# Revit family: Nursing Bench 3000 height adjustable_v_1.0
name_source: partatom
category: Specialty Equipment
revit_build: Autodesk Revit Architecture 2012 (Build: 20110309_2315(x64)
units: mm (PartAtom-declared; Revit-internal decimal feet)

## types (4) — shared parameters
Adjustment Interval (Height) = 300 mm - 1000 mm above floor
Assembly Code = C1030200
Assembly Description = Bath & Toilet Accessories
Couch Elevation = 865 mm  [stored 2.83793 ft]
File Version = V 1.0
Manufacturer = Pressalit Care
OmniClass Number = 23.40.20.21
OmniClass Title = Toilet and Bath Specialties
URL = www.pressalitcare.com

## per-type parameters (varying)
| type | Bed Pattern 1300 | Bed Pattern 1800 | Description | Length | Model | Rail | With Safety Rail |
| Height adjustable nursing bench with safety rail, 1800 mm. Electric. | No | Yes | Nursing bench with safety rail. Couch 1910 x 798 mm. 700 mm height adjustable. | 1800 mm  [stored 5.90551 ft] | R8538 | 1600 mm  [stored 5.24934 ft] | Yes |
| Height adjustable nursing bench with safety rail, 1300 mm. Electric. | Yes | No | Nursing bench with safety rail. Couch 1410 x 798 mm. 700 mm height adjustable. | 1300 mm  [stored 4.26509 ft] | R8533 | 1200 mm | Yes |
| Height adjustable nursing bench, 1300 mm. Electric. | Yes | No | Nursing bench. Couch 1410 x 798 mm. 700 mm height adjustable. | 1300 mm  [stored 4.26509 ft] | R8513 | 1200 mm | No |
| Height adjustable nursing bench, 1800 mm. Electric. | No | Yes | Nursing bench. Couch 1910 x 798 mm. 700 mm height adjustable. | 1800 mm  [stored 5.90551 ft] | R8518 | 1600 mm  [stored 5.24934 ft] | No |

note: [stored X ft] marks values corroborated as IEEE doubles in the binary element streams (Revit-internal decimal feet)

## geometry (parser evidence)
native form markers: Blend x4, Sweep x4
no freeform markers — native parametric forms only
